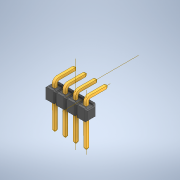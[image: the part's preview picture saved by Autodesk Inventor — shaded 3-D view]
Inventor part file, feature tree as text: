
AUTODESK INVENTOR PART (.ipt)
format: ipt  version: 2020 (Build 240168000, 168)  size: 340,480 bytes
history: native  units: in
note: dims shown in document units (in); Inventor stores cm internally (conversion verified against a paired STEP export)
features: other x13, plane x6
ambient origin geometry x8: Origin, YZ Plane, XZ Plane, XY Plane, X Axis, Y Axis, Z Axis, Center Point
bodies: Solid1 (feature_tree), Solid2 (feature_tree), Solid3 (feature_tree), Solid4 (feature_tree), Solid5 (feature_tree), Solid6 (feature_tree), Solid7 (feature_tree)
feature tree (19):
  other  "brep_1"
  plane  "Work Plane1"
  plane  "Work Plane2"
  plane  "Work Plane6"
  plane  "Work Plane3"
  other  "Work Axis1"
  other  "Work Axis2"
  other  "Work Axis4"
  other  "Work Axis5"
  plane  "Work Plane4"
  plane  "Work Plane5"
  other  "brep_2"
  other  "brep_3"
  other  "brep_4"
  other  "brep_5"
  other  "brep_6"
  other  "brep_7"
  other  "Composite1"
  other  "Srf1"
